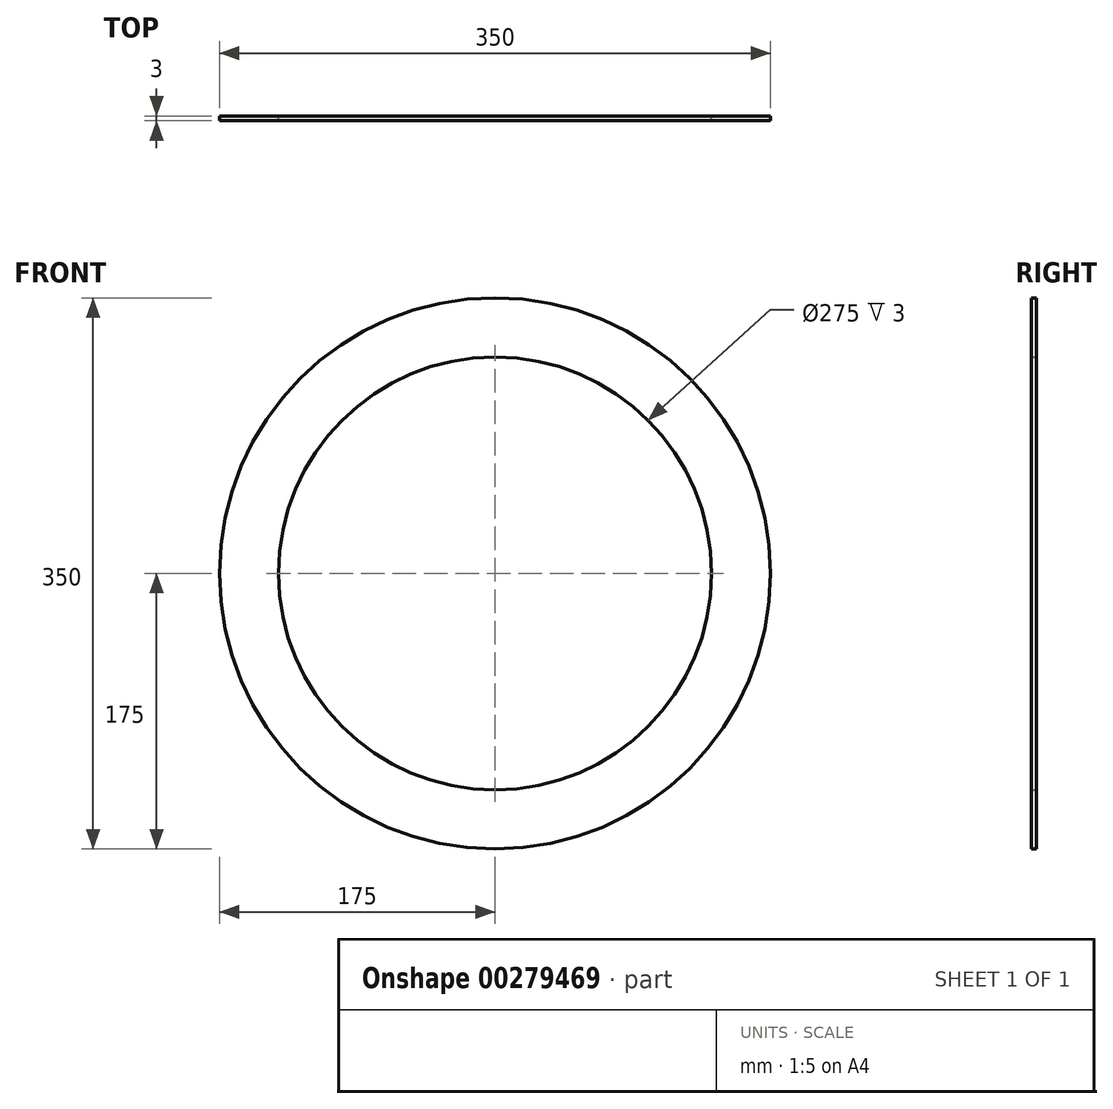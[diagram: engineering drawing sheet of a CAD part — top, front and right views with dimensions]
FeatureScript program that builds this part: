
annotation { "Feature Type Name" : "Feature", "Feature Type Description" : "" }
export const myFeature = defineFeature(function(context is Context, id is Id, definition is map)
    precondition{}
    {
        {
            var Q0;
            Q0=qCreatedBy(makeId("Front.planeOp"),FACE);
            var sketch = newSketch(context, id + "F0", { "sketchPlane" : qUnion([Q0])});
            skCircle(sketch, "E0", {"center": v(0, 0) * mm, "radius": 175 * mm});
            skCircle(sketch, "E1", {"center": v(0, 0) * mm, "radius": 137.5 * mm});
            skSolve(sketch);
        }
        {
            var Q0;
            Q0 = qSketchRegion(id + "F0", true);
            extrude(context, id + "F1", {"entities" : qUnion([Q0]), "depth" : 3 * mm});
        }
    });
